# Revit family: BOX RL
name_source: partatom
category: Modelos genéricos
revit_build: Autodesk Revit 2017 (Build: 20160225_1515(x64)
units: mm (PartAtom-declared; Revit-internal decimal feet)

## family parameters
Compartido = No
Corte con vacíos al cargar = No
Cota de conector redondo = Diámetro de uso
Puede alojar armadura = No
Punto de cálculo de habitación = No
Se basa en plano de trabajo = No
Siempre vertical = Sí
Tipo de pieza = Normal

## types (7) — shared parameters
EspPeu = 3 mm  [stored 0.00984252 ft]
Fabricante = Casals Ventilación
G = 74 mm  [stored 0.242782 ft]
HPeu = 60 mm  [stored 0.19685 ft]
URL = www.casals.com
esp = 2 mm  [stored 0.00656168 ft]
material = <Por categoría>

## per-type parameters (varying)
| type | A | B | D | Dimensiones | F | H | L | a | dNOM | f |
| BOX RL 400 | 800 mm  [stored 2.62467 ft] | 800 mm  [stored 2.62467 ft] | 696 mm  [stored 2.28346 ft] | 1002x860x874 | 398 mm  [stored 1.30577 ft] | 1002 mm  [stored 3.2874 ft] | 559 mm | 52 mm | 400 mm  [stored 1.31234 ft] | 395 mm  [stored 1.29593 ft] |
| BOX RL 450 | 800 mm  [stored 2.62467 ft] | 800 mm  [stored 2.62467 ft] | 696 mm  [stored 2.28346 ft] | 1002x860x874 | 448 mm  [stored 1.46982 ft] | 1002 mm  [stored 3.2874 ft] | 559 mm | 52 mm | 450 mm  [stored 1.47638 ft] | 445 mm  [stored 1.45997 ft] |
| BOX RL 500 | 925 mm  [stored 3.03478 ft] | 925 mm  [stored 3.03478 ft] | 821 mm  [stored 2.69357 ft] | 1127x985x999 | 498 mm  [stored 1.63386 ft] | 1127 mm  [stored 3.69751 ft] | 683 mm  [stored 2.24081 ft] | 52 mm | 500 mm  [stored 1.64042 ft] | 495 mm  [stored 1.62402 ft] |
| BOX RL 560 | 925 mm  [stored 3.03478 ft] | 925 mm  [stored 3.03478 ft] | 821 mm  [stored 2.69357 ft] | 1127x985x999 | 548 mm  [stored 1.7979 ft] | 1127 mm  [stored 3.69751 ft] | 683 mm  [stored 2.24081 ft] | 52 mm | 550 mm | 545 mm  [stored 1.78806 ft] |
| BOX RL 630 | 1000 mm  [stored 3.28084 ft] | 1000 mm  [stored 3.28084 ft] | 892 mm  [stored 2.92651 ft] | 1203x1060x1074 | 628 mm  [stored 2.06037 ft] | 1203 mm | 758 mm  [stored 2.48688 ft] | 54 mm | 630 mm  [stored 2.06693 ft] | 625 mm  [stored 2.05052 ft] |
| BOX RL 710 | 1000 mm  [stored 3.28084 ft] | 1000 mm  [stored 3.28084 ft] | 892 mm  [stored 2.92651 ft] | 1203x1060x1074 | 698 mm  [stored 2.29003 ft] | 1203 mm | 758 mm  [stored 2.48688 ft] | 54 mm | 700 mm | 695 mm  [stored 2.28018 ft] |
| BOX RL 800 | 1060 mm  [stored 3.47769 ft] | 1060 mm  [stored 3.47769 ft] | 952 mm  [stored 3.12336 ft] | 1262x1120x1134 | 798 mm  [stored 2.61811 ft] | 1262 mm | 817 mm  [stored 2.68045 ft] | 54 mm | 800 mm  [stored 2.62467 ft] | 795 mm  [stored 2.60827 ft] |

note: [stored X ft] marks values corroborated as IEEE doubles in the binary element streams (Revit-internal decimal feet)
